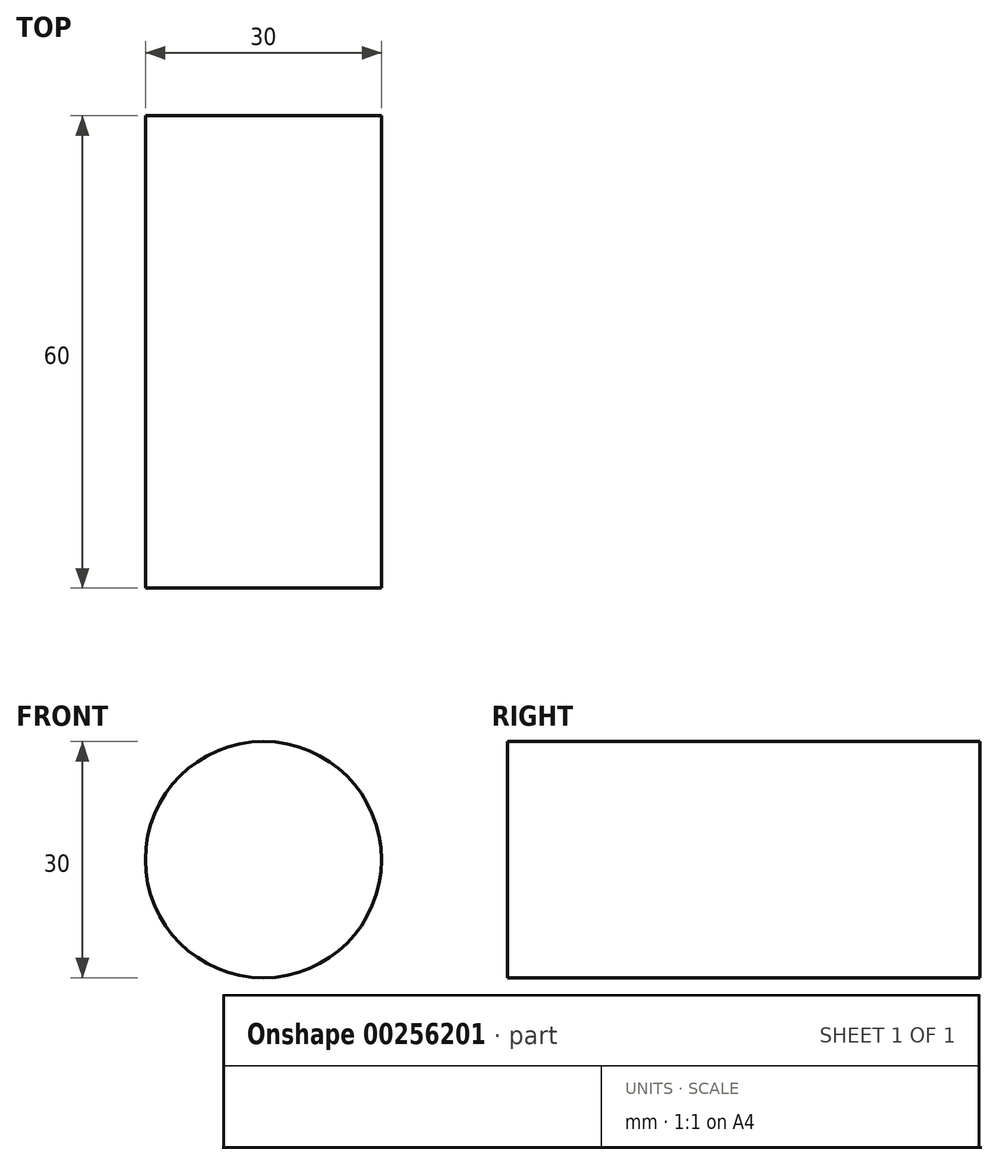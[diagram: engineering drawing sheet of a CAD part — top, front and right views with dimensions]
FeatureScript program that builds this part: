
annotation { "Feature Type Name" : "Feature", "Feature Type Description" : "" }
export const myFeature = defineFeature(function(context is Context, id is Id, definition is map)
    precondition{}
    {
        {
            var Q0;
            Q0=qCreatedBy(makeId("Front.planeOp"),FACE);
            var sketch = newSketch(context, id + "F0", { "sketchPlane" : qUnion([Q0])});
            skCircle(sketch, "E0", {"center": v(0, 0) * mm, "radius": 15 * mm});
            skSolve(sketch);
        }
        {
            var Q0;
            Q0 = qSketchRegion(id + "F0", true);
            var Q1;
            Q1=makeQuery(id+"F0.imprint","IMPRINT",FACE,{"disambiguationData":[TD([[makeQuery(id+"F0.imprint","IMPRINT",EDGE,{"derivedFrom":sQuery(id+"F0.wireOp",EDGE,"E0")}),1.0]])]});
            extrude(context, id + "F1", {"entities" : qUnion([Q0, Q1]), "depth" : 60 * mm});
        }
    });
